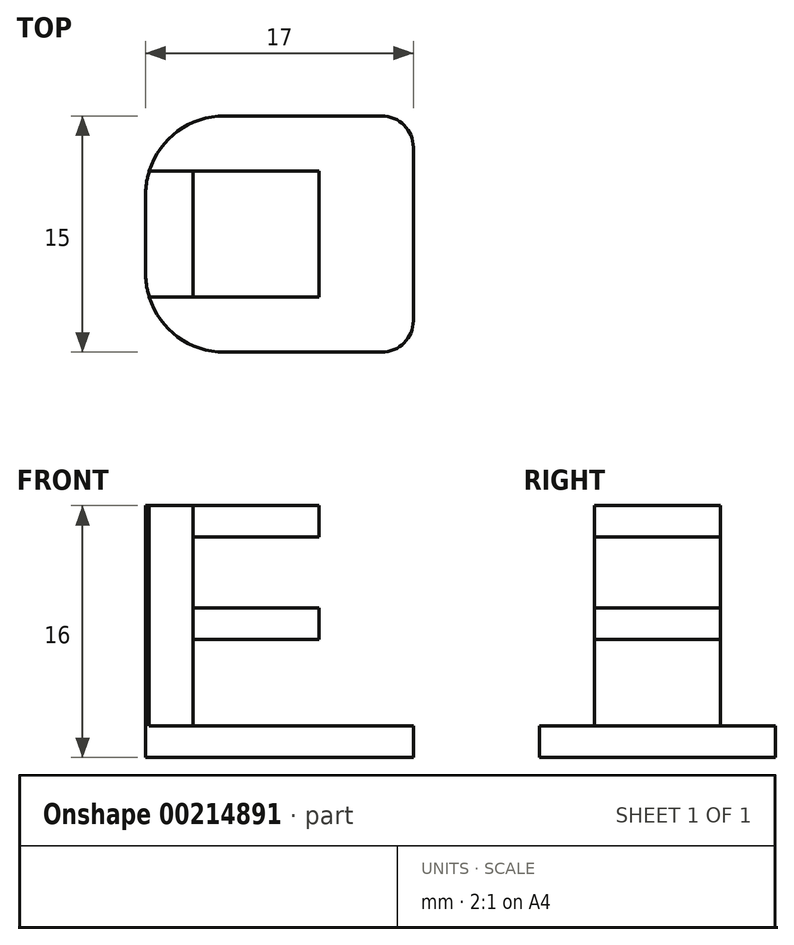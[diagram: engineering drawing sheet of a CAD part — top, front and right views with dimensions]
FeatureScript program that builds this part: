
annotation { "Feature Type Name" : "Feature", "Feature Type Description" : "" }
export const myFeature = defineFeature(function(context is Context, id is Id, definition is map)
    precondition{}
    {
        {
            var Q0;
            Q0=qCreatedBy(makeId("Top.planeOp"),FACE);
            var sketch = newSketch(context, id + "F0", { "sketchPlane" : qUnion([Q0])});
            skLineSegment(sketch, "E0", {"start": v(-39.3, -15) * mm, "end": v(-22.3, -15) * mm});
            skLineSegment(sketch, "E1", {"start": v(-22.3, -15) * mm, "end": v(-22.3, 0) * mm});
            skLineSegment(sketch, "E2", {"start": v(-39.3, -15) * mm, "end": v(-39.3, 0) * mm});
            skLineSegment(sketch, "E3", {"start": v(-39.3, 0) * mm, "end": v(-22.3, 0) * mm});
            skSolve(sketch);
        }
        {
            var Q0;
            Q0=makeQuery(id+"F0.imprint","IMPRINT",FACE,{"disambiguationData":[TD([[makeQuery(id+"F0.imprint","IMPRINT",EDGE,{"derivedFrom":sQuery(id+"F0.wireOp",EDGE,"E0")}),1.0]])]});
            extrude(context, id + "F1", {"entities" : qUnion([Q0]), "depth" : 2 * mm});
        }
        {
            var Q0;
            Q0=makeQuery(id+"F1.opExtrude","SWEPT_FACE",FACE,{"disambiguationData":[OSD([sQuery(id+"F0.wireOp",EDGE,"E2")])]});
            var sketch = newSketch(context, id + "F2", { "sketchPlane" : qUnion([Q0])});
            skLineSegment(sketch, "E4", {"start": v(7.5, 2) * mm, "end": v(3.5, 2) * mm});
            skLineSegment(sketch, "E5", {"start": v(7.5, 2) * mm, "end": v(11.5, 2) * mm});
            skPoint(sketch, "E6.end.orphan", {"position": v(7.5, 11) * mm});
            skLineSegment(sketch, "E7", {"start": v(3.5, 2) * mm, "end": v(3.5, 16) * mm});
            skPoint(sketch, "E8.start.orphan", {"position": v(3.5, 11) * mm});
            skPoint(sketch, "E9.end.orphan", {"position": v(11.5, 11) * mm});
            skLineSegment(sketch, "E10", {"start": v(11.5, 2) * mm, "end": v(11.5, 16) * mm});
            skLineSegment(sketch, "E11", {"start": v(3.5, 16) * mm, "end": v(11.5, 16) * mm});
            skSolve(sketch);
        }
        {
            var Q0;
            Q0=makeQuery(id+"F2.imprint","IMPRINT",FACE,{"disambiguationData":[TD([[makeQuery(id+"F2.imprint","IMPRINT",EDGE,{"derivedFrom":sQuery(id+"F2.wireOp",EDGE,"E4")}),-1.0]])]});
            extrude(context, id + "F3", {"entities" : qUnion([Q0]), "operationType" : NewBodyOperationType.ADD, "oppositeDirection" : true, "depth" : 3 * mm});
        }
        {
            var Q0;
            Q0=makeQuery(id+"F3.opExtrude","SWEPT_FACE",FACE,{"disambiguationData":[OSD([sQuery(id+"F2.wireOp",EDGE,"E7")])]});
            var sketch = newSketch(context, id + "F4", { "sketchPlane" : qUnion([Q0])});
            skLineSegment(sketch, "E12", {"start": v(36.3, 16) * mm, "end": v(36.3, 14) * mm});
            skLineSegment(sketch, "E13", {"start": v(36.3, 16) * mm, "end": v(28.3, 16) * mm});
            skLineSegment(sketch, "E14", {"start": v(28.3, 16) * mm, "end": v(28.3, 14) * mm});
            skLineSegment(sketch, "E15", {"start": v(28.3, 14) * mm, "end": v(36.3, 14) * mm});
            skLineSegment(sketch, "E16", {"start": v(36.3, 14) * mm, "end": v(36.3, 9.5) * mm});
            skLineSegment(sketch, "E17", {"start": v(36.3, 9.5) * mm, "end": v(28.3, 9.5) * mm});
            skLineSegment(sketch, "E18", {"start": v(28.3, 9.5) * mm, "end": v(28.3, 7.5) * mm});
            skLineSegment(sketch, "E19", {"start": v(28.3, 7.5) * mm, "end": v(36.3, 7.5) * mm});
            skSolve(sketch);
        }
        {
            var Q0;
            {var subQ0=sQuery(id+"F4.wireOp",EDGE,"E17");Q0=makeQuery(id+"F4.imprint","IMPRINT",FACE,{"disambiguationData":[TD([[makeQuery(id+"F4.imprint","IMPRINT",EDGE,{"derivedFrom":subQ0}),1.0]])]});}
            var Q1;
            Q1=makeQuery(id+"F4.imprint","IMPRINT",FACE,{"disambiguationData":[TD([[makeQuery(id+"F4.imprint","IMPRINT",EDGE,{"derivedFrom":sQuery(id+"F4.wireOp",EDGE,"E12")}),1.0]])]});
            extrude(context, id + "F5", {"entities" : qUnion([Q0, Q1]), "oppositeDirection" : true, "depth" : 8 * mm});
        }
        {
            var Q0;
            Q0=makeQuery(id+"F1.opExtrude","SWEPT_EDGE",EDGE,{"disambiguationData":[OSD([sQuery(id+"F0.wireOp",EDGE,"E2"),sQuery(id+"F0.wireOp",EDGE,"E3")])]});
            var Q1;
            Q1=makeQuery(id+"F1.opExtrude","SWEPT_EDGE",EDGE,{"disambiguationData":[OSD([sQuery(id+"F0.wireOp",EDGE,"E0"),sQuery(id+"F0.wireOp",EDGE,"E2")])]});
            fillet(context, id + "F6", {"entities" : qUnion([Q0, Q1]), "radius" : 5 * mm, "tangentPropagation" : true, "allowEdgeOverflow" : false});
        }
        {
            var Q0;
            Q0=makeQuery(id+"F1.opExtrude","SWEPT_EDGE",EDGE,{"disambiguationData":[OSD([sQuery(id+"F0.wireOp",EDGE,"E0"),sQuery(id+"F0.wireOp",EDGE,"E1")])]});
            var Q1;
            Q1=makeQuery(id+"F1.opExtrude","SWEPT_EDGE",EDGE,{"disambiguationData":[OSD([sQuery(id+"F0.wireOp",EDGE,"E1"),sQuery(id+"F0.wireOp",EDGE,"E3")])]});
            fillet(context, id + "F7", {"entities" : qUnion([Q0, Q1]), "radius" : 2 * mm, "tangentPropagation" : true, "allowEdgeOverflow" : false});
        }
    });
